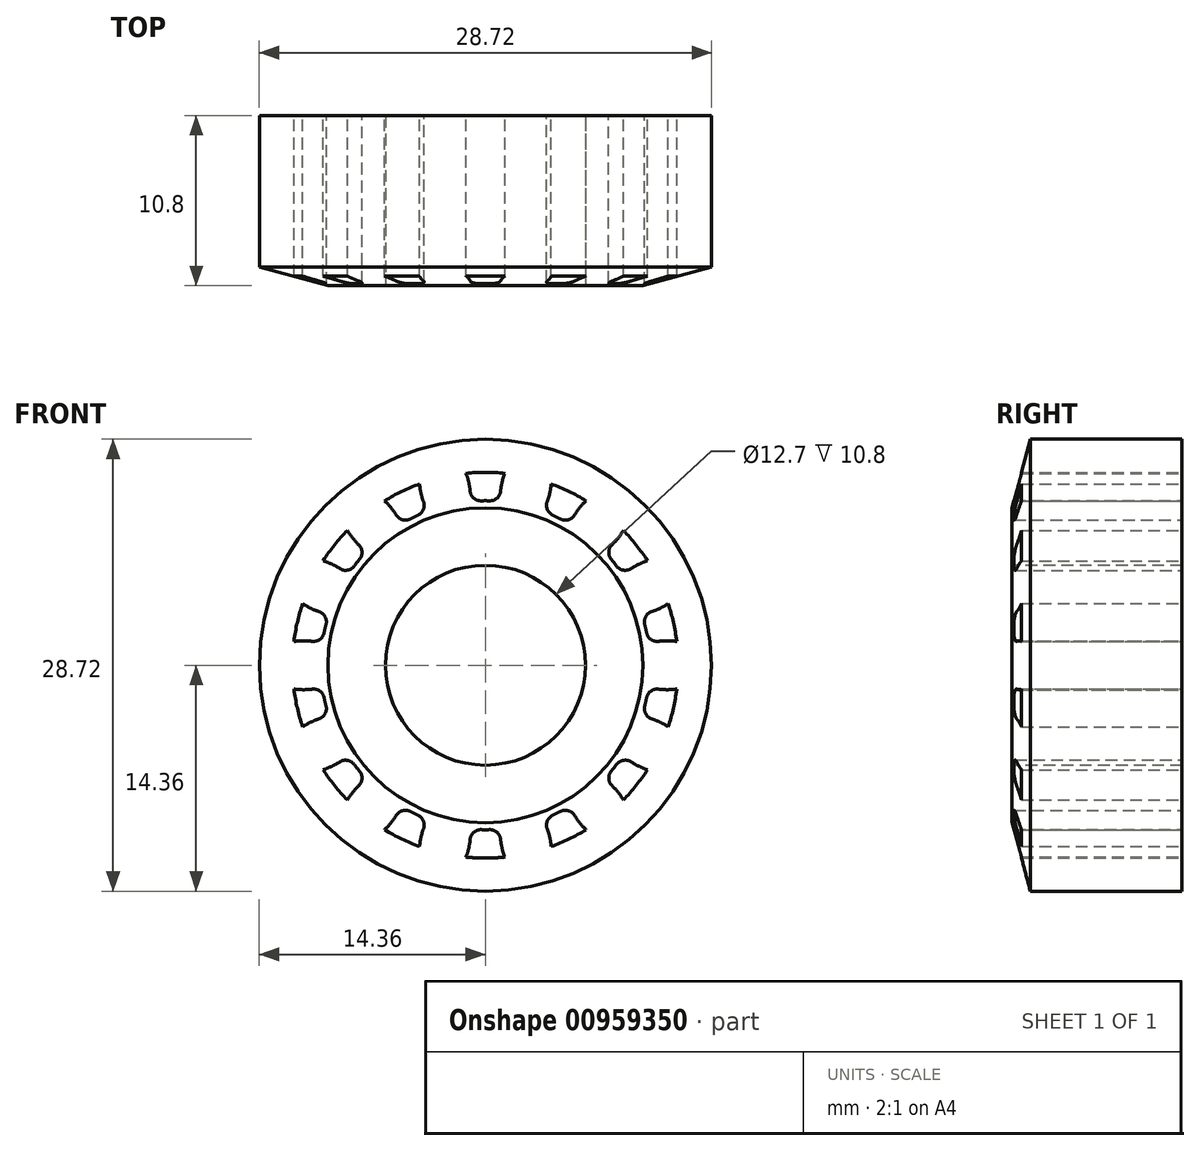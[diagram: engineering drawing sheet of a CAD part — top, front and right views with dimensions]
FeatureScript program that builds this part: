
annotation { "Feature Type Name" : "Feature", "Feature Type Description" : "" }
export const myFeature = defineFeature(function(context is Context, id is Id, definition is map)
    precondition{}
    {
        {
            assignVariable(context, id + "F0", {"name" : "mn", "anyValue" : 1.75});
        }
        {
            assignVariable(context, id + "F1", {"name" : "Zaehnezahl", "anyValue" : 14});
        }
        {
            assignVariable(context, id + "F2", {"name" : "Breite", "anyValue" : 10.8});
        }
        {
            assignVariable(context, id + "F3", {"name" : "Zahnfussradius", "anyValue" : 0.38 * getVariable(context, 'mn')});
        }
        {
            var Q0;
            Q0=qCreatedBy(makeId("Front.planeOp"),FACE);
            var sketch = newSketch(context, id + "F4", { "sketchPlane" : qUnion([Q0])});
            skCircle(sketch, "E0", {"center": v(0, 0) * mm, "radius": 10.45 * mm});
            skArc(sketch, "E1", {"start": v(2.72, 14.1) * mm, "mid": v(1.36, 12.48) * mm, "end": v(0.96, 10.4) * mm});
            skPoint(sketch, "E2", {"position": v(1.23, 12.19) * mm});
            skArc(sketch, "E3.MirrorCS", {"start": v(-2.72, 14.1) * mm, "mid": v(-1.36, 12.48) * mm, "end": v(-0.96, 10.4) * mm});
            skPoint(sketch, "E4.MirrorP", {"position": v(-1.23, 12.19) * mm});
            skLineSegment(sketch, "E5", {"start": v(3.2, 14) * mm, "end": v(0, 0) * mm, "construction": true});
            skArc(sketch, "E6.MirrorCS", {"start": v(3.67, 13.88) * mm, "mid": v(4.2, 11.83) * mm, "end": v(3.65, 9.79) * mm});
            skPoint(sketch, "E7.MirrorP", {"position": v(4.18, 11.52) * mm});
            skLineSegment(sketch, "E8.MirrorCS", {"start": v(-3.2, 14) * mm, "end": v(0, 0) * mm, "construction": true});
            skArc(sketch, "E9", {"start": v(2.72, 14.1) * mm, "mid": v(-3.2, -14) * mm, "end": v(3.67, 13.88) * mm});
            skArc(sketch, "E10", {"start": v(3.67, 13.88) * mm, "mid": v(3.2, 14) * mm, "end": v(2.72, 14.1) * mm});
            skArc(sketch, "E11", {"start": v(1.23, 12.19) * mm, "mid": v(-2.73, -11.94) * mm, "end": v(4.18, 11.52) * mm});
            skArc(sketch, "E12", {"start": v(4.18, 11.52) * mm, "mid": v(2.73, 11.94) * mm, "end": v(1.23, 12.19) * mm});
            skLineSegment(sketch, "E13", {"start": v(0, 0) * mm, "end": v(0, 12.25) * mm, "construction": true});
            skSolve(sketch);
        }
        {
            var Q0;
            Q0=qCreatedBy(makeId("Front.planeOp"),FACE);
            var sketch = newSketch(context, id + "F5", { "sketchPlane" : qUnion([Q0])});
            skCircle(sketch, "E14", {"center": v(0, 0) * mm, "radius": 14.36 * mm});
            skSolve(sketch);
        }
        {
            var Q0;
            Q0=qSketchRegion(id+"F5",true);
            extrude(context, id + "F6", {"entities" : qUnion([Q0]), "depth" : (getVariable(context, 'Breite')) * mm, "offsetDistance" : 25 * mm});
        }
        {
            var Q0;
            {var subQ0=sQuery(id+"F4.wireOp",EDGE,"E9");var subQ5=sQuery(id+"F4.wireOp",EDGE,"E3.MirrorCS");var subQ6=makeQuery(id+"F4.imprint","INTERSECT",VERTEX,{"derivedFrom":[subQ5,subQ0]});Q0=makeQuery(id+"F4.imprint","IMPRINT",FACE,{"disambiguationData":[TD([[makeQuery(id+"F4.imprint","IMPRINT",EDGE,{"disambiguationData":[TD([[subQ6,-1.0]])],"derivedFrom":subQ5}),1.0]])]});}
            var Q1;
            {var subQ0=sQuery(id+"F4.wireOp",EDGE,"E1");var subQ1=sQuery(id+"F4.wireOp",EDGE,"E0");var subQ2=makeQuery(id+"F4.imprint","INTERSECT",VERTEX,{"derivedFrom":[subQ1,subQ0]});Q1=makeQuery(id+"F4.imprint","IMPRINT",FACE,{"disambiguationData":[TD([[makeQuery(id+"F4.imprint","IMPRINT",EDGE,{"disambiguationData":[TD([[subQ2,-1.0]])],"derivedFrom":subQ1}),-1.0]])]});}
            extrude(context, id + "F7", {"entities" : qUnion([Q0, Q1]), "depth" : (getVariable(context, 'Breite')) * mm, "offsetDistance" : 25 * mm});
        }
        {
            var Q0;
            Q0=makeQuery(id+"F7.opExtrude","SWEPT_EDGE",EDGE,{"disambiguationData":[OSD([sQuery(id+"F4.wireOp",EDGE,"E0"),sQuery(id+"F4.wireOp",EDGE,"E1")])]});
            var Q1;
            Q1=makeQuery(id+"F7.opExtrude","SWEPT_EDGE",EDGE,{"disambiguationData":[OSD([sQuery(id+"F4.wireOp",EDGE,"E0"),sQuery(id+"F4.wireOp",EDGE,"E3.MirrorCS")])]});
            fillet(context, id + "F8", {"entities" : qUnion([Q0, Q1]), "radius" : (getVariable(context, 'Zahnfussradius')) * mm, "tangentPropagation" : true, "allowEdgeOverflow" : false});
        }
        {
            var Q0;
            Q0=makeQuery(id+"F7.opExtrude","SWEPT_BODY",BODY,{"disambiguationData":[OSD([sQuery(id+"F4.wireOp",EDGE,"E0"),sQuery(id+"F4.wireOp",EDGE,"E1"),sQuery(id+"F4.wireOp",EDGE,"E3.MirrorCS"),sQuery(id+"F4.wireOp",EDGE,"E9")])]});
            var Q1;
            Q1=makeQuery(id+"F6.opExtrude","SWEPT_FACE",FACE,{"disambiguationData":[OSD([sQuery(id+"F5.wireOp",EDGE,"E14")])]});
            circularPattern(context, id + "F9", {"operationType" : NewBodyOperationType.REMOVE, "entities" : qUnion([Q0]), "axis" : qUnion([Q1]), "angle" : 360 * degree, "instanceCount" : getVariable(context, 'Zaehnezahl'), "equalSpace" : true, "computeTransformsWithoutBuiltin" : true});
        }
        {
            var Q0;
            Q0=qCreatedBy(makeId("Top.planeOp"),FACE);
            var sketch = newSketch(context, id + "F10", { "sketchPlane" : qUnion([Q0])});
            skLineSegment(sketch, "E15", {"start": v(0, 0) * mm, "end": v(0, -26.25) * mm, "construction": true});
            skLineSegment(sketch, "E16.bottom", {"start": v(0, 0) * mm, "end": v(-6.35, 0) * mm});
            skLineSegment(sketch, "E16.top", {"start": v(0, -10.8) * mm, "end": v(-6.35, -10.8) * mm});
            skLineSegment(sketch, "E16.left", {"start": v(0, 0) * mm, "end": v(0, -10.8) * mm});
            skLineSegment(sketch, "E16.right", {"start": v(-6.35, 0) * mm, "end": v(-6.35, -10.8) * mm});
            skLineSegment(sketch, "E17", {"start": v(-10, -10.8) * mm, "end": v(-14.36, -10.8) * mm});
            skLineSegment(sketch, "E18", {"start": v(-14.36, -10.8) * mm, "end": v(-14.36, -9.63) * mm});
            skLineSegment(sketch, "E19", {"start": v(-14.36, -9.63) * mm, "end": v(-10, -10.8) * mm});
            skSolve(sketch);
        }
        {
            var Q0;
            Q0=makeQuery(id+"F10.imprint","IMPRINT",FACE,{"disambiguationData":[TD([[makeQuery(id+"F10.imprint","IMPRINT",EDGE,{"derivedFrom":sQuery(id+"F10.wireOp",EDGE,"E17")}),-1.0]])]});
            var Q1;
            Q1=makeQuery(id+"F10.imprint","IMPRINT",FACE,{"disambiguationData":[TD([[makeQuery(id+"F10.imprint","IMPRINT",EDGE,{"derivedFrom":sQuery(id+"F10.wireOp",EDGE,"E16.bottom")}),1.0]])]});
            var Q2;
            Q2=sQuery(id+"F10.wireOp",EDGE,"E15");
            revolve(context, id + "F11", {"operationType" : NewBodyOperationType.REMOVE, "surfaceOperationType" : NewSurfaceOperationType.NEW, "entities" : qUnion([Q0, Q1]), "axis" : qUnion([Q2]), "revolveType" : RevolveType.FULL, "oppositeDirection" : true});
        }
    });
